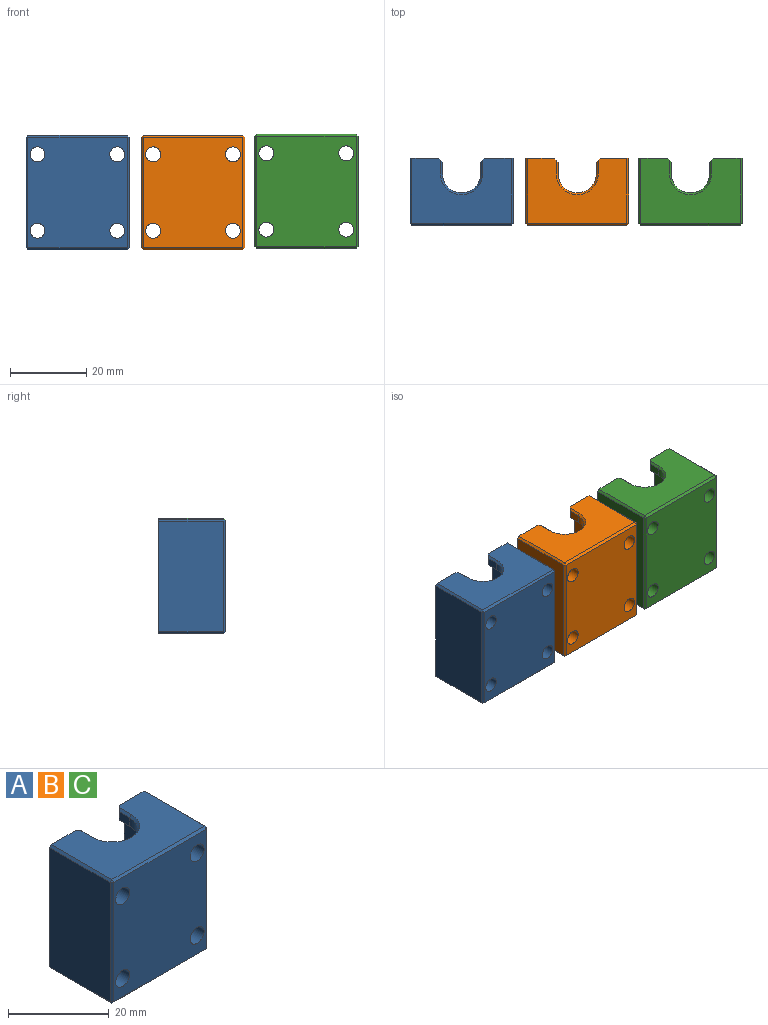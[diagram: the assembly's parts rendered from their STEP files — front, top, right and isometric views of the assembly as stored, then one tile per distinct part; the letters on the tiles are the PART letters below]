
ASSEMBLY  parts=3 mates=2
PART A: 50 faces, bbox 27x17.5x30 mm
  f0: plane 29x26mm, normal (0,-1,0), area 706.2mm2, adj f18,f19,f20,f21,f33,f38,f39,f43
  f1: plane 26x17mm, normal (0,0,-1), area 350.2mm2, adj f13,f17,f23,f24,f26,f27,f28,f34
  f2: plane 29x17mm, normal (-1,0,0), area 493mm2, adj f17,f37,f40,f43
  f3: plane 29x17mm, normal (1,0,0), area 493mm2, adj f13,f32,f33,f34
  f4: plane 26x17mm, normal (0,0,1), area 350.2mm2, adj f13,f17,f22,f25,f29,f30,f31,f32
  f5: cylinder r=7.5mm len=23.86mm, axis (0,0,-1), area 562.2mm2, adj f7,f9,f10,f14
  f6: cylinder r=5mm len=10mm, axis (0,0,-1), area 32.5mm2, adj f12,f15,f27,f45
  f7: plane 15x11.5mm, normal (0,0,1), area 56.6mm2, adj f5,f10,f13,f14,f17,f23,f24,f44
  f8: cylinder r=5mm len=10mm, axis (0,0,1), area 32.5mm2, adj f11,f16,f30,f48
  f9: plane 15x11.5mm, normal (0,0,-1), area 56.6mm2, adj f5,f10,f13,f14,f17,f22,f25,f47
  f10: plane 23.86x4mm, normal (-1,0,0), area 95.4mm2, adj f5,f7,f9,f13
  f11: plane 3x2.07mm, normal (-1,0,0), area 6.2mm2, adj f8,f22,f29,f49
  f12: plane 3x2.07mm, normal (-1,0,0), area 6.2mm2, adj f6,f24,f28,f46
  f13: plane 30x7.5mm, normal (0,1,0), area 165.1mm2, adj f1,f3,f4,f7,f9,f10,f20,f21
  f14: plane 23.86x4mm, normal (1,0,0), area 95.4mm2, adj f5,f7,f9,f17
  f15: plane 3x2.07mm, normal (1,0,0), area 6.2mm2, adj f6,f23,f26,f44
  f16: plane 3x2.07mm, normal (1,0,0), area 6.2mm2, adj f8,f25,f31,f47
  f17: plane 30x7.5mm, normal (0,1,0), area 165.1mm2, adj f1,f2,f4,f7,f9,f14,f18,f19
  f18: cylinder r=1.95mm len=17.5mm, axis (0,1,0), area 214.4mm2, adj f0,f17
  f19: cylinder r=1.95mm len=17.5mm, axis (0,1,0), area 214.4mm2, adj f0,f17
  f20: cylinder r=1.95mm len=17.5mm, axis (0,1,0), area 214.4mm2, adj f0,f13
  f21: cylinder r=1.95mm len=17.5mm, axis (0,1,0), area 214.4mm2, adj f0,f13
  f22: plane 3.07x1mm, normal (-0.71,0.71,0), area 4mm2, adj f4,f9,f11,f13,f29,f49
  f23: plane 3.07x1mm, normal (0.71,0.71,0), area 4mm2, adj f1,f7,f15,f17,f26,f44
  f24: plane 3.07x1mm, normal (-0.71,0.71,0), area 4mm2, adj f1,f7,f12,f13,f28,f46
  f25: plane 3.07x1mm, normal (0.71,0.71,0), area 4mm2, adj f4,f9,f16,f17,f31,f47
  f26: plane 3.5x0.5mm, normal (0.71,0,-0.71), area 2.3mm2, adj f1,f15,f23,f27
  f27: cone r=5mm half-angle=45deg, axis (0,0,-1), area 11.7mm2, adj f1,f6,f26,f28
  f28: plane 3.5x0.5mm, normal (-0.71,0,-0.71), area 2.3mm2, adj f1,f12,f24,f27
  f29: plane 3.5x0.5mm, normal (-0.71,0,0.71), area 2.3mm2, adj f4,f11,f22,f30
  f30: cone r=5mm half-angle=45deg, axis (0,0,1), area 11.7mm2, adj f4,f8,f29,f31
  f31: plane 3.5x0.5mm, normal (0.71,0,0.71), area 2.3mm2, adj f4,f16,f25,f30
  f32: plane 17x0.5mm, normal (0.71,0,0.71), area 12mm2, adj f3,f4,f13,f35
  f33: plane 29x0.5mm, normal (0.71,-0.71,0), area 20.5mm2, adj f0,f3,f35,f36
  f34: plane 17x0.5mm, normal (0.71,0,-0.71), area 12mm2, adj f1,f3,f13,f36
  f35: plane 0.5x0.5mm, normal (0.58,-0.58,0.58), area 0.2mm2, adj f32,f33,f38
  f36: plane 0.5x0.5mm, normal (0.58,-0.58,-0.58), area 0.2mm2, adj f33,f34,f39
  f37: plane 17x0.5mm, normal (-0.71,0,0.71), area 12mm2, adj f2,f4,f17,f41
  f38: plane 26x0.5mm, normal (0,-0.71,0.71), area 18.4mm2, adj f0,f4,f35,f41
  f39: plane 26x0.5mm, normal (0,-0.71,-0.71), area 18.4mm2, adj f0,f1,f36,f42
  f40: plane 17x0.5mm, normal (-0.71,0,-0.71), area 12mm2, adj f1,f2,f17,f42
  f41: plane 0.5x0.5mm, normal (-0.58,-0.58,0.58), area 0.2mm2, adj f37,f38,f43
  f42: plane 0.5x0.5mm, normal (-0.58,-0.58,-0.58), area 0.2mm2, adj f39,f40,f43
  f43: plane 29x0.5mm, normal (-0.71,-0.71,0), area 20.5mm2, adj f0,f2,f41,f42
  f44: plane 3.5x0.5mm, normal (0.71,0,0.71), area 2.3mm2, adj f7,f15,f23,f45
  f45: cone r=5.5mm half-angle=45deg, axis (0,0,1), area 11.7mm2, adj f6,f7,f44,f46
  f46: plane 3.5x0.5mm, normal (-0.71,0,0.71), area 2.3mm2, adj f7,f12,f24,f45
  f47: plane 3.5x0.5mm, normal (0.71,0,-0.71), area 2.3mm2, adj f9,f16,f25,f48
  f48: cone r=5.5mm half-angle=45deg, axis (0,0,-1), area 11.7mm2, adj f8,f9,f47,f49
  f49: plane 3.5x0.5mm, normal (-0.71,0,-0.71), area 2.3mm2, adj f9,f11,f22,f48
PART B: same geometry as A
PART C: same geometry as A
PLACE A t=(-74.14,23.44,-1.91)mm
PLACE B t=(-43.84,23.44,-1.91)mm
PLACE C t=(-14.2,23.44,-1.63)mm
MATE planar B.f0 <-> A.f0  axis (0,-1,0) through (-39.25,-16.83,13.09)mm
MATE planar C.f0 <-> A.f0  axis (0,-1,0) through (-9.61,-16.83,13.37)mm
